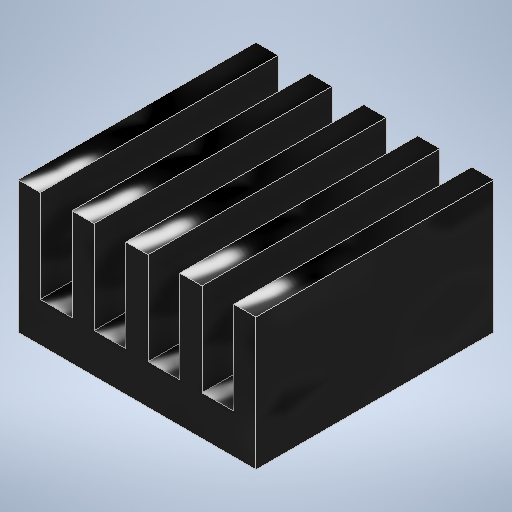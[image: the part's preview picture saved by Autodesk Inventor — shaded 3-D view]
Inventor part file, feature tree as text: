
AUTODESK INVENTOR PART (.ipt)
format: ipt  version: 2025 (Build 290162000, 162)  size: 247,296 bytes
history: native  units: mm
features: extrude x1, sketch x1
ambient origin geometry x8: Origin, YZ Plane, XZ Plane, XY Plane, X Axis, Y Axis, Z Axis, Center Point
bodies: Solid1 (feature_tree)
feature tree (2):
  extrude  "Extrusion1"  Depth=5.0mm
  sketch  "Sketch1"  dims[d0=9.0mm d2=5.0mm d3=1.2mm d4=3.5mm d5=9.0mm d6=0.0mm]
